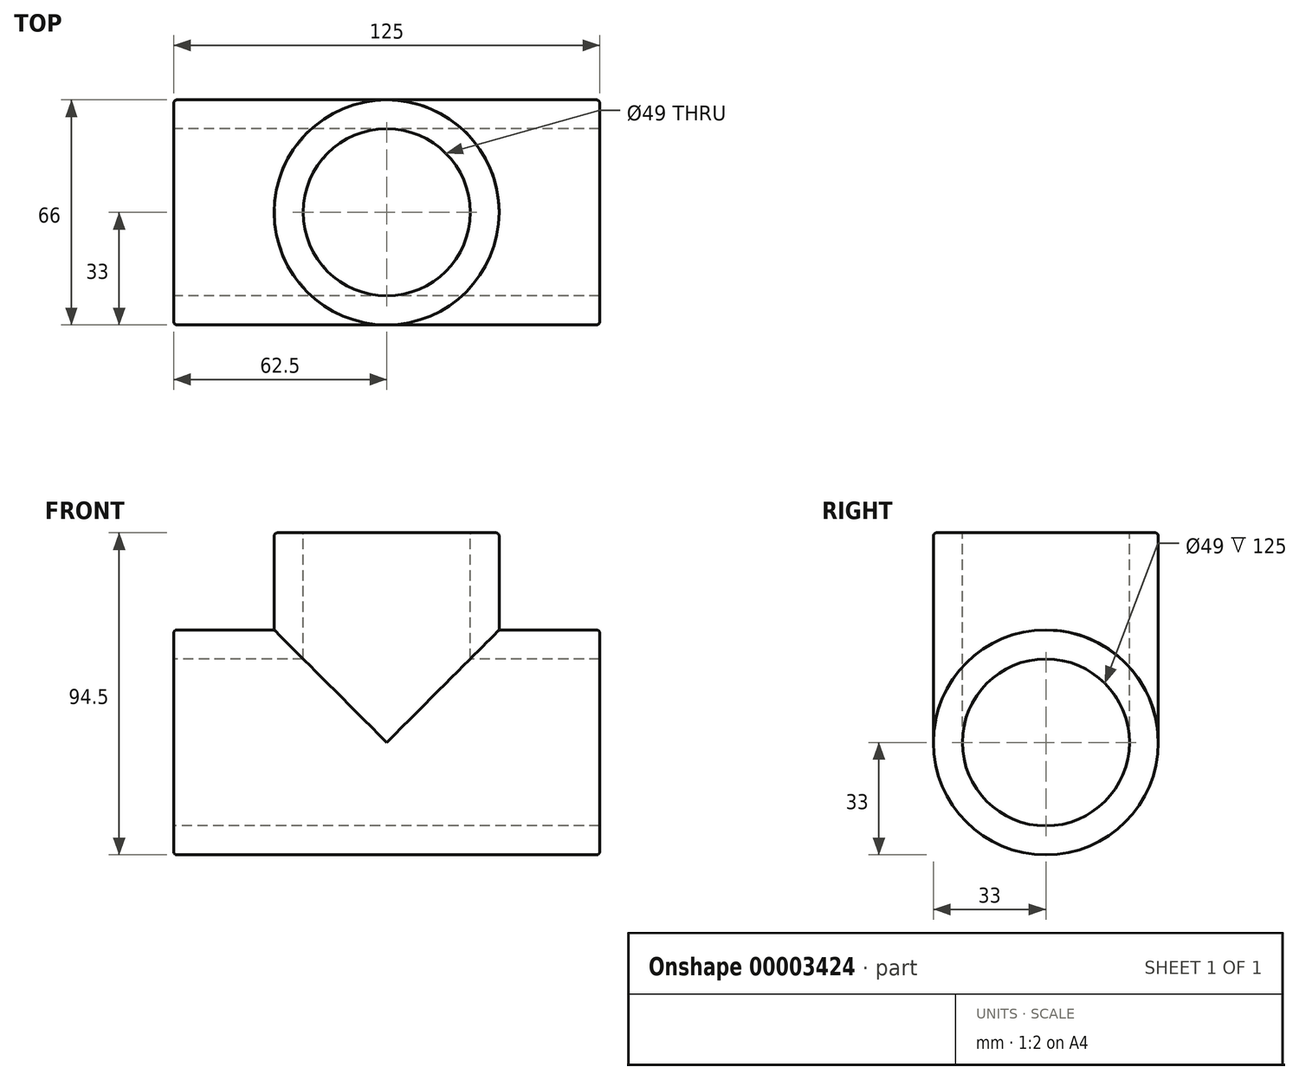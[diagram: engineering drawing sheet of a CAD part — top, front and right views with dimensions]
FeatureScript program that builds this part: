
annotation { "Feature Type Name" : "Feature", "Feature Type Description" : "" }
export const myFeature = defineFeature(function(context is Context, id is Id, definition is map)
    precondition{}
    {
        {
            var Q0;
            Q0=qCreatedBy(makeId("Right.planeOp"),FACE);
            var sketch = newSketch(context, id + "F0", { "sketchPlane" : qUnion([Q0])});
            skCircle(sketch, "E0", {"center": v(0, 0) * mm, "radius": 33 * mm});
            skSolve(sketch);
        }
        {
            var Q0;
            Q0 = qSketchRegion(id + "F0", true);
            extrude(context, id + "F1", {"entities" : qUnion([Q0]), "endBound" : BoundingType.SYMMETRIC, "depth" : 125 * mm});
        }
        {
            var Q0;
            Q0=qCreatedBy(makeId("Front.planeOp"),FACE);
            var sketch = newSketch(context, id + "F2", { "sketchPlane" : qUnion([Q0])});
            skLineSegment(sketch, "E1", {"start": v(-64.5, 61.5) * mm, "end": v(68.68, 61.5) * mm, "construction": true});
            skLineSegment(sketch, "E2.0", {"start": v(-62.5, 33) * mm, "end": v(-62.5, -33) * mm, "construction": true});
            skSolve(sketch);
        }
        {
            var Q0;
            Q0=qCreatedBy(makeId("Top.planeOp"),FACE);
            var Q1;
            Q1=sQuery(id+"F2.wireOp",VERTEX,"E1.start");
            cPlane(context, id + "F3", {"entities" : qUnion([Q0, Q1]), "cplaneType" : CPlaneType.PLANE_POINT, "offset" : 150 * mm, "width" : 150 * mm, "height" : 150 * mm});
        }
        {
            var Q0;
            Q0=qCreatedBy(id+"F3.planeOp",FACE);
            var sketch = newSketch(context, id + "F4", { "sketchPlane" : qUnion([Q0])});
            skCircle(sketch, "E3", {"center": v(0, 0) * mm, "radius": 33 * mm});
            skLineSegment(sketch, "E4.0", {"start": v(-62.5, 33) * mm, "end": v(-62.5, -33) * mm, "construction": true});
            skLineSegment(sketch, "E5", {"start": v(-62.5, 33) * mm, "end": v(63.36, 33) * mm, "construction": true});
            skSolve(sketch);
        }
        {
            var Q0;
            Q0 = qSketchRegion(id + "F4", true);
            var Q1;
            Q1=makeQuery(id+"F1.opExtrude","SWEPT_FACE",FACE,{"disambiguationData":[OSD([sQuery(id+"F0.wireOp",EDGE,"E0")])]});
            extrude(context, id + "F5", {"entities" : qUnion([Q0]), "operationType" : NewBodyOperationType.ADD, "endBound" : BoundingType.UP_TO_BODY, "oppositeDirection" : true, "endBoundEntityBody" : qUnion([Q1]), "depth" : 25 * mm});
        }
        {
            var Q0;
            Q0=makeQuery(id+"F5.opExtrude","CAP_FACE",FACE,{"disambiguationData":[OSD([sQuery(id+"F4.wireOp",EDGE,"E3")])],"isStart":true});
            var Q1;
            Q1=makeQuery(id+"F1.opExtrude","CAP_FACE",FACE,{"disambiguationData":[OSD([sQuery(id+"F0.wireOp",EDGE,"E0")])],"isStart":true});
            var Q2;
            Q2=makeQuery(id+"F1.opExtrude","CAP_FACE",FACE,{"disambiguationData":[OSD([sQuery(id+"F0.wireOp",EDGE,"E0")])],"isStart":false});
            shell(context, id + "F6", {"entities" : qUnion([Q0, Q1, Q2]), "thickness" : 8.5 * mm});
        }
        {
            var Q0;
            Q0=makeQuery(id+"F5.opExtrude","CAP_EDGE",EDGE,{"disambiguationData":[OSD([sQuery(id+"F4.wireOp",EDGE,"E3")]),OD(0.0)],"isStart":false});
            var Q1;
            Q1=makeQuery(id+"F5.opExtrude","CAP_EDGE",EDGE,{"disambiguationData":[OSD([sQuery(id+"F4.wireOp",EDGE,"E3")]),OD(1.0)],"isStart":false});
            var Q2;
            {var subQ0=sQuery(id+"F4.wireOp",EDGE,"E3");Q2=makeQuery(id+"F6.opShell","OFFSET_EDGE",EDGE,{"disambiguationData":[OSD([subQ0]),TDD([makeQuery(id+"F5.opExtrude","CAP_EDGE",EDGE,{"disambiguationData":[OSD([subQ0]),OD(0.0)],"isStart":false})])]});}
            var Q3;
            {var subQ0=sQuery(id+"F4.wireOp",EDGE,"E3");Q3=makeQuery(id+"F6.opShell","OFFSET_EDGE",EDGE,{"disambiguationData":[OSD([subQ0]),TDD([makeQuery(id+"F5.opExtrude","CAP_EDGE",EDGE,{"disambiguationData":[OSD([subQ0]),OD(1.0)],"isStart":false})])]});}
            fillet(context, id + "F7", {"entities" : qUnion([Q0, Q1, Q2, Q3]), "radius" : 0.5 * mm, "tangentPropagation" : true, "allowEdgeOverflow" : false});
        }
        {
            var Q0;
            Q0=makeQuery(id+"F1.opExtrude","CAP_EDGE",EDGE,{"disambiguationData":[OSD([sQuery(id+"F0.wireOp",EDGE,"E0")])],"isStart":true});
            var Q1;
            Q1=makeQuery(id+"F1.opExtrude","CAP_EDGE",EDGE,{"disambiguationData":[OSD([sQuery(id+"F0.wireOp",EDGE,"E0")])],"isStart":false});
            var Q2;
            Q2=makeQuery(id+"F5.opExtrude","CAP_EDGE",EDGE,{"disambiguationData":[OSD([sQuery(id+"F4.wireOp",EDGE,"E3")])],"isStart":true});
            fillet(context, id + "F8", {"entities" : qUnion([Q0, Q1, Q2]), "radius" : 1 * mm, "tangentPropagation" : true, "allowEdgeOverflow" : false});
        }
    });
